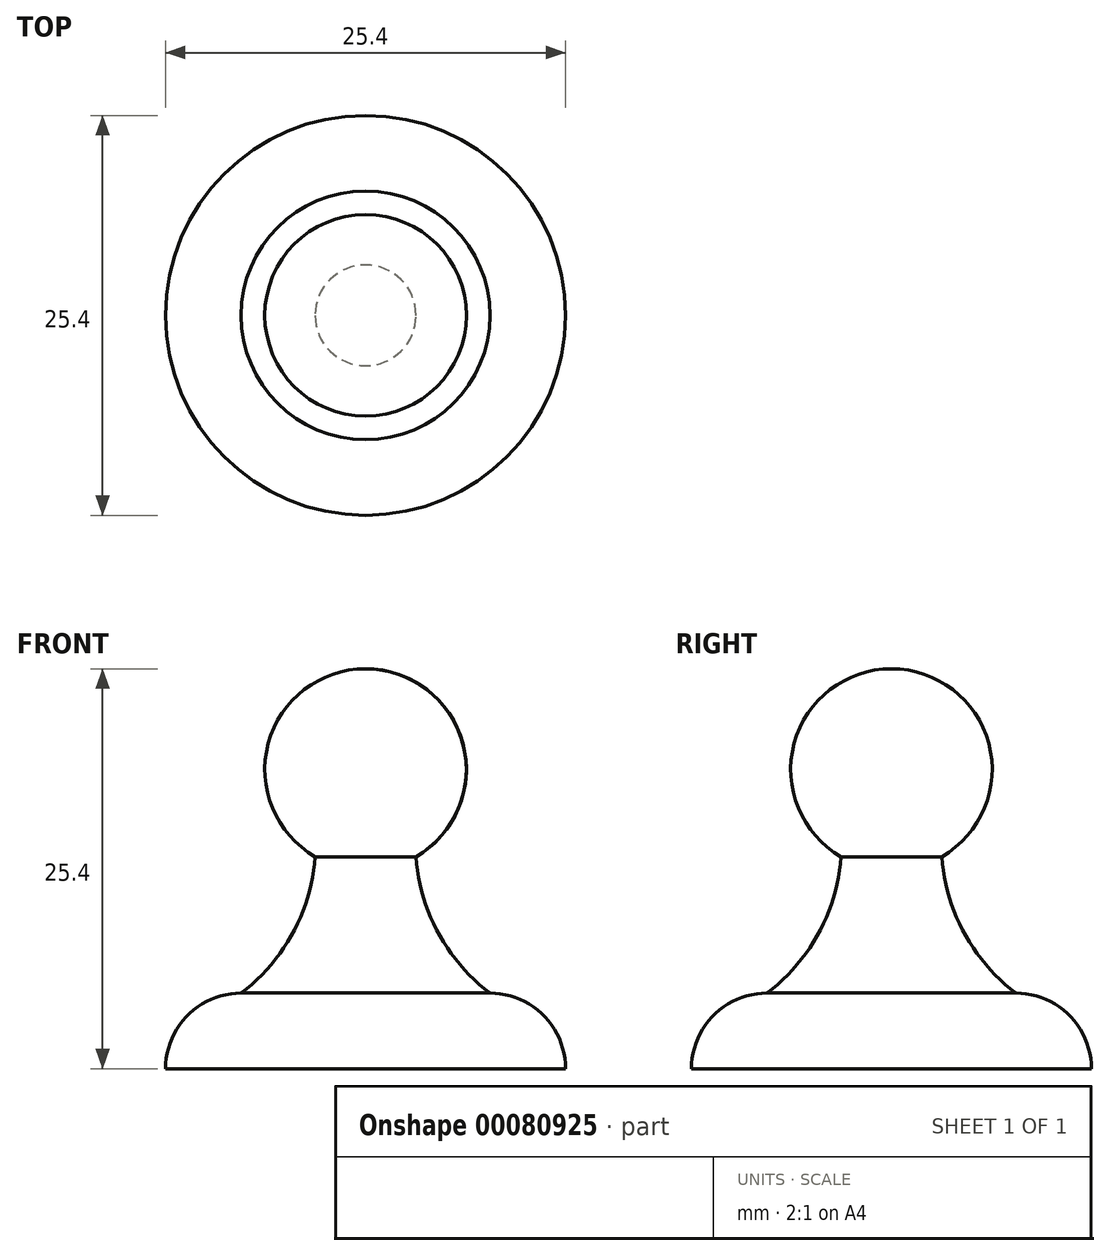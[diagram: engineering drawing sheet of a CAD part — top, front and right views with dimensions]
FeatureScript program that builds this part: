
annotation { "Feature Type Name" : "Feature", "Feature Type Description" : "" }
export const myFeature = defineFeature(function(context is Context, id is Id, definition is map)
    precondition{}
    {
        {
            var Q0;
            Q0=qCreatedBy(makeId("Front.planeOp"),FACE);
            var sketch = newSketch(context, id + "F0", { "sketchPlane" : qUnion([Q0])});
            skLineSegment(sketch, "E0", {"start": v(0, 0) * mm, "end": v(0, 25.4) * mm});
            skLineSegment(sketch, "E1", {"start": v(0, 0) * mm, "end": v(12.7, 0) * mm});
            skArc(sketch, "E2", {"start": v(12.7, 0) * mm, "mid": v(11.3, 3.4) * mm, "end": v(7.9, 4.8) * mm});
            skArc(sketch, "E3", {"start": v(0, 25.4) * mm, "mid": v(6.18, 20.66) * mm, "end": v(3.2, 13.46) * mm});
            skArc(sketch, "E4", {"start": v(3.2, 13.46) * mm, "mid": v(4.62, 8.62) * mm, "end": v(7.9, 4.8) * mm});
            skSolve(sketch);
        }
        {
            var Q0;
            Q0=qSketchRegion(id+"F0",true);
            var Q1;
            Q1=sQuery(id+"F0.wireOp",EDGE,"E0");
            revolve(context, id + "F1", {"entities" : qUnion([Q0]), "axis" : qUnion([Q1]), "revolveType" : RevolveType.FULL});
        }
    });
